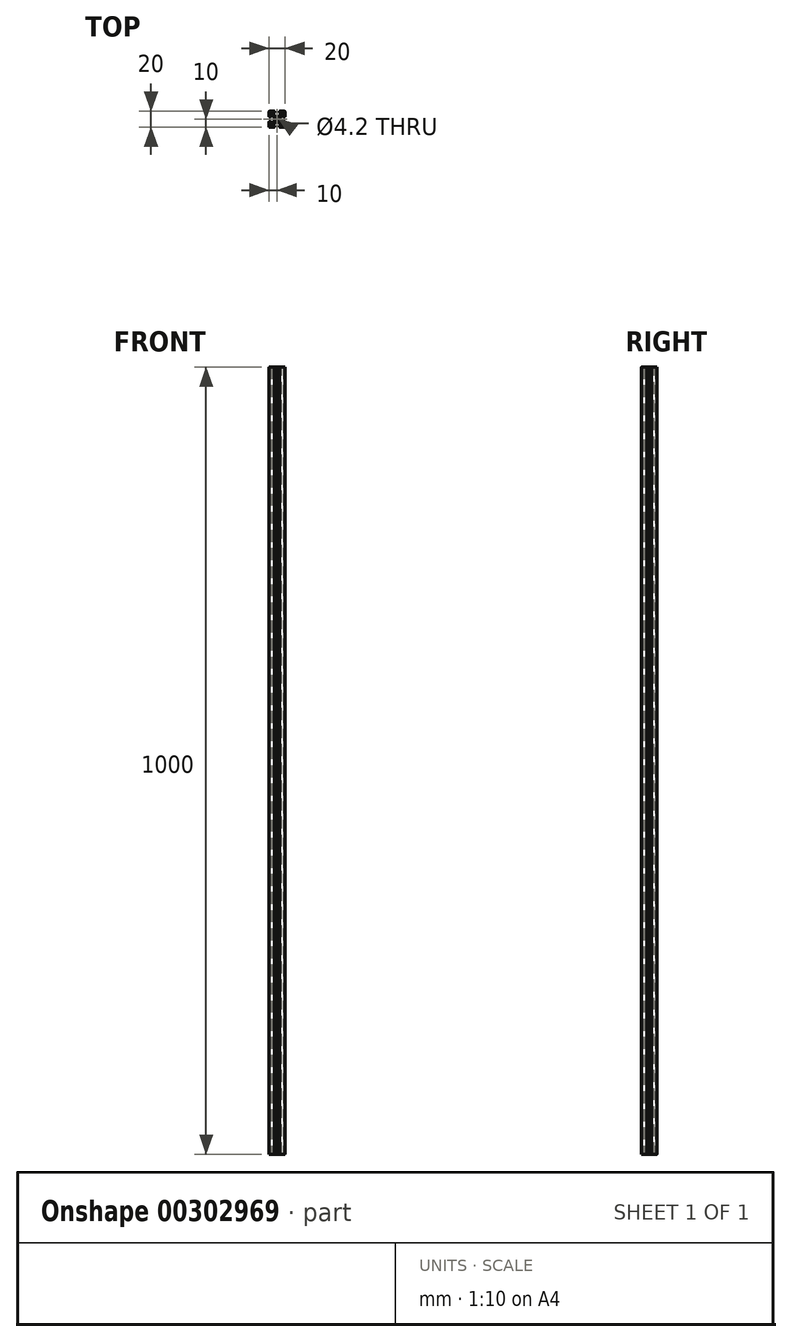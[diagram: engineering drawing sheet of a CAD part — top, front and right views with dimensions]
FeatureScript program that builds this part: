
annotation { "Feature Type Name" : "Feature", "Feature Type Description" : "" }
export const myFeature = defineFeature(function(context is Context, id is Id, definition is map)
    precondition{}
    {
        {
            var Q0;
            Q0=qCreatedBy(makeId("Top.planeOp"),FACE);
            var sketch = newSketch(context, id + "F0", { "sketchPlane" : qUnion([Q0])});
            skLineSegment(sketch, "E0.bottom", {"start": v(10, 10) * mm, "end": v(3.1, 10) * mm});
            skLineSegment(sketch, "E0.top", {"start": v(10, -10) * mm, "end": v(3.1, -10) * mm});
            skLineSegment(sketch, "E0.left", {"start": v(10, 10) * mm, "end": v(10, 3.1) * mm});
            skLineSegment(sketch, "E0.right", {"start": v(-10, 10) * mm, "end": v(-10, 3.1) * mm});
            skPoint(sketch, "E0.middle", {"position": v(0, 0) * mm});
            skLineSegment(sketch, "E1.0", {"start": v(6.59, -8) * mm, "end": v(2.6, -8) * mm});
            skLineSegment(sketch, "E1.1", {"start": v(8, 6.59) * mm, "end": v(8, 2.6) * mm});
            skLineSegment(sketch, "E1.2", {"start": v(6.59, 8) * mm, "end": v(2.6, 8) * mm});
            skLineSegment(sketch, "E1.3", {"start": v(-8, 6.59) * mm, "end": v(-8, 2.6) * mm});
            skCircle(sketch, "E2", {"center": v(0, 0) * mm, "radius": 2.1 * mm});
            skLineSegment(sketch, "E3.bottom", {"start": v(2.09, 3.5) * mm, "end": v(-2.09, 3.5) * mm});
            skLineSegment(sketch, "E3.top", {"start": v(2.09, -3.5) * mm, "end": v(-2.09, -3.5) * mm});
            skLineSegment(sketch, "E3.left", {"start": v(3.5, 2.09) * mm, "end": v(3.5, -2.09) * mm});
            skLineSegment(sketch, "E3.right", {"start": v(-3.5, 2.09) * mm, "end": v(-3.5, -2.09) * mm});
            skLineSegment(sketch, "E4.0", {"start": v(-2.09, 3.5) * mm, "end": v(-6.59, 8) * mm});
            skLineSegment(sketch, "E5.0", {"start": v(-3.5, 2.09) * mm, "end": v(-8, 6.59) * mm});
            skPoint(sketch, "E6.start.orphan", {"position": v(-3.5, 3.5) * mm});
            skLineSegment(sketch, "E7.0", {"start": v(2.09, -3.5) * mm, "end": v(6.59, -8) * mm});
            skLineSegment(sketch, "E8.0", {"start": v(3.5, -2.09) * mm, "end": v(8, -6.59) * mm});
            skLineSegment(sketch, "E9.0", {"start": v(3.5, 2.09) * mm, "end": v(8, 6.59) * mm});
            skLineSegment(sketch, "E10.0", {"start": v(2.09, 3.5) * mm, "end": v(6.59, 8) * mm});
            skLineSegment(sketch, "E11.0", {"start": v(-3.5, -2.09) * mm, "end": v(-8, -6.59) * mm});
            skLineSegment(sketch, "E12.0", {"start": v(-2.09, -3.5) * mm, "end": v(-6.59, -8) * mm});
            skPoint(sketch, "E13.orphan", {"position": v(-3.5, -3.5) * mm});
            skPoint(sketch, "E14.orphan", {"position": v(3.5, -3.5) * mm});
            skPoint(sketch, "E15.orphan", {"position": v(3.5, 3.5) * mm});
            skLineSegment(sketch, "E16.top", {"start": v(3.1, 9.5) * mm, "end": v(2.6, 9.5) * mm});
            skLineSegment(sketch, "E16.left", {"start": v(3.1, 10) * mm, "end": v(3.1, 9.5) * mm});
            skLineSegment(sketch, "E16.right", {"start": v(-3.1, 10) * mm, "end": v(-3.1, 9.5) * mm});
            skPoint(sketch, "E16.middle", {"position": v(0, 10) * mm});
            skPoint(sketch, "E17.orphan", {"position": v(-3.1, 10.5) * mm});
            skLineSegment(sketch, "E18.trimOffspring", {"start": v(-3.1, 10) * mm, "end": v(-10, 10) * mm});
            skPoint(sketch, "E19.orphan", {"position": v(3.1, 10.5) * mm});
            skLineSegment(sketch, "E20.left", {"start": v(2.6, 7.81) * mm, "end": v(2.6, 9.5) * mm});
            skLineSegment(sketch, "E20.right", {"start": v(-2.6, 7.81) * mm, "end": v(-2.6, 9.5) * mm});
            skPoint(sketch, "E20.middle", {"position": v(0, 9.5) * mm});
            skPoint(sketch, "E20.top.end.orphan", {"position": v(-2.6, 11.19) * mm});
            skPoint(sketch, "E21.orphan", {"position": v(2.6, 11.19) * mm});
            skLineSegment(sketch, "E22.trimOffspring", {"start": v(-2.6, 9.5) * mm, "end": v(-3.1, 9.5) * mm});
            skLineSegment(sketch, "E23.trimOffspring", {"start": v(-2.6, 8) * mm, "end": v(-6.59, 8) * mm});
            skLineSegment(sketch, "E24.bottom", {"start": v(10, 3.1) * mm, "end": v(9.5, 3.1) * mm});
            skLineSegment(sketch, "E24.top", {"start": v(10.5, -3.1) * mm, "end": v(9.5, -3.1) * mm});
            skLineSegment(sketch, "E24.right", {"start": v(9.5, 3.1) * mm, "end": v(9.5, 2.6) * mm});
            skPoint(sketch, "E24.middle", {"position": v(10, 0) * mm});
            skLineSegment(sketch, "E25.bottom", {"start": v(9.5, -2.6) * mm, "end": v(7.69, -2.6) * mm});
            skLineSegment(sketch, "E25.top", {"start": v(9.5, 2.6) * mm, "end": v(7.69, 2.6) * mm});
            skPoint(sketch, "E26.orphan", {"position": v(12.31, 2.6) * mm});
            skPoint(sketch, "E27.orphan", {"position": v(10.5, 3.1) * mm});
            skPoint(sketch, "E28.orphan", {"position": v(12.31, -2.6) * mm});
            skLineSegment(sketch, "E29.trimOffspring", {"start": v(10, -3.1) * mm, "end": v(10, -10) * mm});
            skLineSegment(sketch, "E30.trimOffspring", {"start": v(8, -2.6) * mm, "end": v(8, -6.59) * mm});
            skLineSegment(sketch, "E31.trimOffspring", {"start": v(9.5, -2.6) * mm, "end": v(9.5, -3.1) * mm});
            skLineSegment(sketch, "E32.bottom", {"start": v(3.1, -9.5) * mm, "end": v(2.6, -9.5) * mm});
            skLineSegment(sketch, "E32.left", {"start": v(3.1, -9.5) * mm, "end": v(3.1, -10) * mm});
            skLineSegment(sketch, "E32.right", {"start": v(-3.1, -9.5) * mm, "end": v(-3.1, -10) * mm});
            skPoint(sketch, "E32.middle", {"position": v(0, -10) * mm});
            skLineSegment(sketch, "E33.right", {"start": v(-2.6, -9.5) * mm, "end": v(-2.6, -8) * mm});
            skPoint(sketch, "E34.orphan", {"position": v(-2.6, -7.1) * mm});
            skPoint(sketch, "E35.orphan", {"position": v(2.6, -7.1) * mm});
            skLineSegment(sketch, "E36.trimOffspring", {"start": v(-2.6, -8) * mm, "end": v(-6.59, -8) * mm});
            skLineSegment(sketch, "E37.trimOffspring", {"start": v(-2.6, -9.5) * mm, "end": v(-3.1, -9.5) * mm});
            skLineSegment(sketch, "E38.trimOffspring", {"start": v(2.6, -9.5) * mm, "end": v(2.6, -8) * mm});
            skLineSegment(sketch, "E39.trimOffspring", {"start": v(-3.1, -10) * mm, "end": v(-10, -10) * mm});
            skPoint(sketch, "E33.bottom.start.orphan", {"position": v(2.6, -12.9) * mm});
            skPoint(sketch, "E40.orphan", {"position": v(-2.6, -12.9) * mm});
            skPoint(sketch, "E41.orphan", {"position": v(-3.1, -10.5) * mm});
            skPoint(sketch, "E42.orphan", {"position": v(3.1, -10.5) * mm});
            skLineSegment(sketch, "E43.bottom", {"start": v(-10, 3.1) * mm, "end": v(-9.5, 3.1) * mm});
            skLineSegment(sketch, "E43.top", {"start": v(-10, -3.1) * mm, "end": v(-9.5, -3.1) * mm});
            skLineSegment(sketch, "E43.right", {"start": v(-9.5, 3.1) * mm, "end": v(-9.5, 2.6) * mm});
            skPoint(sketch, "E43.middle", {"position": v(-10, 0) * mm});
            skLineSegment(sketch, "E44.bottom", {"start": v(-7.74, -2.6) * mm, "end": v(-9.5, -2.6) * mm});
            skLineSegment(sketch, "E44.top", {"start": v(-7.74, 2.6) * mm, "end": v(-9.5, 2.6) * mm});
            skPoint(sketch, "E45.orphan", {"position": v(-12.26, 2.6) * mm});
            skPoint(sketch, "E46.orphan", {"position": v(-12.26, -2.6) * mm});
            skLineSegment(sketch, "E47.trimOffspring", {"start": v(-10, -3.1) * mm, "end": v(-10, -10) * mm});
            skPoint(sketch, "E48.orphan", {"position": v(-10.5, -3.1) * mm});
            skPoint(sketch, "E49.orphan", {"position": v(-10.5, 3.1) * mm});
            skLineSegment(sketch, "E50.trimOffspring", {"start": v(-9.5, -2.6) * mm, "end": v(-9.5, -3.1) * mm});
            skLineSegment(sketch, "E51.trimOffspring", {"start": v(-8, -2.6) * mm, "end": v(-8, -6.59) * mm});
            skSolve(sketch);
        }
        {
            var Q0;
            Q0=makeQuery(id+"F0.imprint","IMPRINT",FACE,{"disambiguationData":[TD([[makeQuery(id+"F0.imprint","IMPRINT",EDGE,{"derivedFrom":sQuery(id+"F0.wireOp",EDGE,"E0.bottom")}),1.0]])]});
            extrude(context, id + "F1", {"entities" : qUnion([Q0]), "depth" : 1000 * mm});
        }
        {
            var Q0;
            Q0=makeQuery(id+"F1.opExtrude","SWEPT_EDGE",EDGE,{"disambiguationData":[OSD([sQuery(id+"F0.wireOp",EDGE,"E0.right"),sQuery(id+"F0.wireOp",EDGE,"E18.trimOffspring")])]});
            var Q1;
            Q1=makeQuery(id+"F1.opExtrude","SWEPT_EDGE",EDGE,{"disambiguationData":[OSD([sQuery(id+"F0.wireOp",EDGE,"E39.trimOffspring"),sQuery(id+"F0.wireOp",EDGE,"E47.trimOffspring")])]});
            var Q2;
            Q2=makeQuery(id+"F1.opExtrude","SWEPT_EDGE",EDGE,{"disambiguationData":[OSD([sQuery(id+"F0.wireOp",EDGE,"E0.top"),sQuery(id+"F0.wireOp",EDGE,"E29.trimOffspring")])]});
            var Q3;
            Q3=makeQuery(id+"F1.opExtrude","SWEPT_EDGE",EDGE,{"disambiguationData":[OSD([sQuery(id+"F0.wireOp",EDGE,"E0.bottom"),sQuery(id+"F0.wireOp",EDGE,"E0.left")])]});
            var Q4;
            Q4=makeQuery(id+"F1.opExtrude","SWEPT_EDGE",EDGE,{"disambiguationData":[OSD([sQuery(id+"F0.wireOp",EDGE,"E1.2"),sQuery(id+"F0.wireOp",EDGE,"E10.0")])]});
            var Q5;
            Q5=makeQuery(id+"F1.opExtrude","SWEPT_EDGE",EDGE,{"disambiguationData":[OSD([sQuery(id+"F0.wireOp",EDGE,"E1.1"),sQuery(id+"F0.wireOp",EDGE,"E9.0")])]});
            var Q6;
            Q6=makeQuery(id+"F1.opExtrude","SWEPT_EDGE",EDGE,{"disambiguationData":[OSD([sQuery(id+"F0.wireOp",EDGE,"E1.3"),sQuery(id+"F0.wireOp",EDGE,"E5.0")])]});
            var Q7;
            Q7=makeQuery(id+"F1.opExtrude","SWEPT_EDGE",EDGE,{"disambiguationData":[OSD([sQuery(id+"F0.wireOp",EDGE,"E4.0"),sQuery(id+"F0.wireOp",EDGE,"E23.trimOffspring")])]});
            var Q8;
            Q8=makeQuery(id+"F1.opExtrude","SWEPT_EDGE",EDGE,{"disambiguationData":[OSD([sQuery(id+"F0.wireOp",EDGE,"E12.0"),sQuery(id+"F0.wireOp",EDGE,"E36.trimOffspring")])]});
            var Q9;
            Q9=makeQuery(id+"F1.opExtrude","SWEPT_EDGE",EDGE,{"disambiguationData":[OSD([sQuery(id+"F0.wireOp",EDGE,"E11.0"),sQuery(id+"F0.wireOp",EDGE,"E51.trimOffspring")])]});
            var Q10;
            Q10=makeQuery(id+"F1.opExtrude","SWEPT_EDGE",EDGE,{"disambiguationData":[OSD([sQuery(id+"F0.wireOp",EDGE,"E8.0"),sQuery(id+"F0.wireOp",EDGE,"E30.trimOffspring")])]});
            var Q11;
            Q11=makeQuery(id+"F1.opExtrude","SWEPT_EDGE",EDGE,{"disambiguationData":[OSD([sQuery(id+"F0.wireOp",EDGE,"E1.0"),sQuery(id+"F0.wireOp",EDGE,"E7.0")])]});
            var Q12;
            Q12=makeQuery(id+"F1.opExtrude","SWEPT_EDGE",EDGE,{"disambiguationData":[OSD([sQuery(id+"F0.wireOp",EDGE,"E1.2"),sQuery(id+"F0.wireOp",EDGE,"E20.left")])]});
            var Q13;
            Q13=makeQuery(id+"F1.opExtrude","SWEPT_EDGE",EDGE,{"disambiguationData":[OSD([sQuery(id+"F0.wireOp",EDGE,"E1.1"),sQuery(id+"F0.wireOp",EDGE,"E25.top")])]});
            var Q14;
            Q14=makeQuery(id+"F1.opExtrude","SWEPT_EDGE",EDGE,{"disambiguationData":[OSD([sQuery(id+"F0.wireOp",EDGE,"E25.bottom"),sQuery(id+"F0.wireOp",EDGE,"E30.trimOffspring")])]});
            var Q15;
            Q15=makeQuery(id+"F1.opExtrude","SWEPT_EDGE",EDGE,{"disambiguationData":[OSD([sQuery(id+"F0.wireOp",EDGE,"E44.bottom"),sQuery(id+"F0.wireOp",EDGE,"E51.trimOffspring")])]});
            var Q16;
            Q16=makeQuery(id+"F1.opExtrude","SWEPT_EDGE",EDGE,{"disambiguationData":[OSD([sQuery(id+"F0.wireOp",EDGE,"E33.right"),sQuery(id+"F0.wireOp",EDGE,"E36.trimOffspring")])]});
            var Q17;
            Q17=makeQuery(id+"F1.opExtrude","SWEPT_EDGE",EDGE,{"disambiguationData":[OSD([sQuery(id+"F0.wireOp",EDGE,"E20.right"),sQuery(id+"F0.wireOp",EDGE,"E23.trimOffspring")])]});
            var Q18;
            Q18=makeQuery(id+"F1.opExtrude","SWEPT_EDGE",EDGE,{"disambiguationData":[OSD([sQuery(id+"F0.wireOp",EDGE,"E1.3"),sQuery(id+"F0.wireOp",EDGE,"E44.top")])]});
            var Q19;
            Q19=makeQuery(id+"F1.opExtrude","SWEPT_EDGE",EDGE,{"disambiguationData":[OSD([sQuery(id+"F0.wireOp",EDGE,"E1.0"),sQuery(id+"F0.wireOp",EDGE,"E38.trimOffspring")])]});
            fillet(context, id + "F2", {"entities" : qUnion([Q0, Q1, Q2, Q3, Q4, Q5, Q6, Q7, Q8, Q9, Q10, Q11, Q12, Q13, Q14, Q15, Q16, Q17, Q18, Q19]), "radius" : 0.5 * mm, "tangentPropagation" : true, "allowEdgeOverflow" : false});
        }
    });
